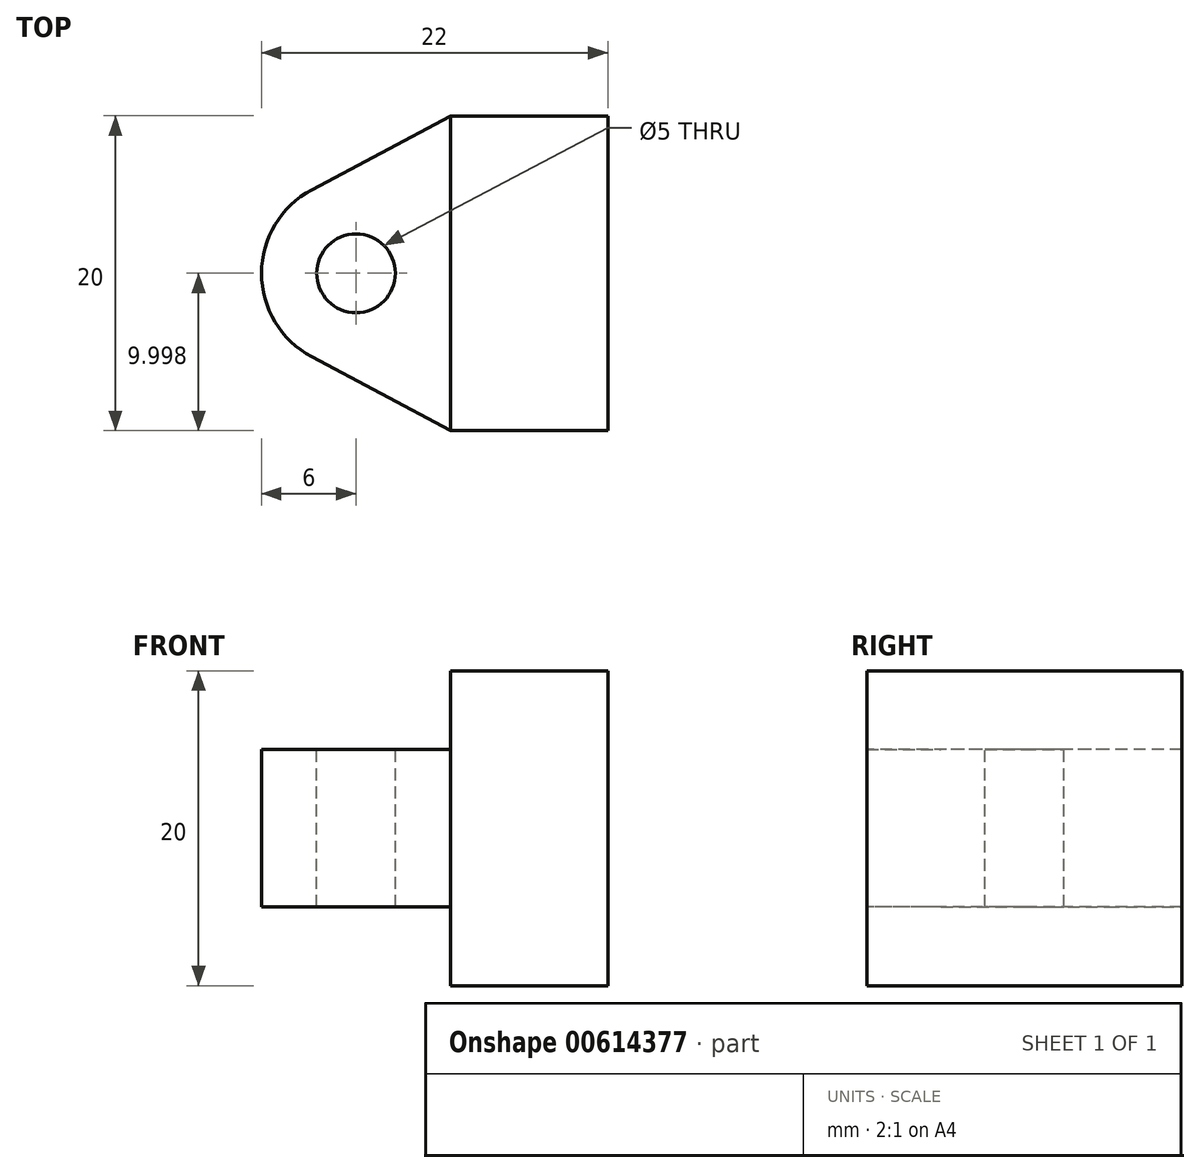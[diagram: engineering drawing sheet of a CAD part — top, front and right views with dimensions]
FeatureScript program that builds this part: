
annotation { "Feature Type Name" : "Feature", "Feature Type Description" : "" }
export const myFeature = defineFeature(function(context is Context, id is Id, definition is map)
    precondition{}
    {
        {
            var Q0;
            Q0=qCreatedBy(makeId("Right.planeOp"),FACE);
            var sketch = newSketch(context, id + "F0", { "sketchPlane" : qUnion([Q0])});
            skLineSegment(sketch, "E0", {"start": v(5.69, -2.66) * mm, "end": v(-14.31, -2.66) * mm});
            skLineSegment(sketch, "E1", {"start": v(-14.31, -2.66) * mm, "end": v(-14.31, -22.66) * mm});
            skLineSegment(sketch, "E2", {"start": v(-14.31, -22.66) * mm, "end": v(5.69, -22.66) * mm});
            skLineSegment(sketch, "E3", {"start": v(5.69, -22.66) * mm, "end": v(5.69, -2.66) * mm});
            skSolve(sketch);
        }
        {
            var Q0;
            Q0=makeQuery(id+"F0.imprint","IMPRINT",FACE,{"disambiguationData":[TD([[makeQuery(id+"F0.imprint","IMPRINT",EDGE,{"derivedFrom":sQuery(id+"F0.wireOp",EDGE,"E0")}),1.0]])]});
            extrude(context, id + "F1", {"entities" : qUnion([Q0]), "depth" : 10 * mm, "offsetDistance" : 25 * mm});
        }
        {
            var Q0;
            Q0=makeQuery(id+"F1.opExtrude","SWEPT_FACE",FACE,{"disambiguationData":[OSD([sQuery(id+"F0.wireOp",EDGE,"E1")])]});
            var sketch = newSketch(context, id + "F2", { "sketchPlane" : qUnion([Q0])});
            skLineSegment(sketch, "E4", {"start": v(0, -7.66) * mm, "end": v(-12, -7.66) * mm});
            skLineSegment(sketch, "E5", {"start": v(-12, -7.66) * mm, "end": v(-12, -17.66) * mm});
            skLineSegment(sketch, "E6", {"start": v(-12, -17.66) * mm, "end": v(0, -17.66) * mm});
            skLineSegment(sketch, "E7", {"start": v(0, -17.66) * mm, "end": v(0, -7.66) * mm});
            skSolve(sketch);
        }
        {
            var Q0;
            Q0=makeQuery(id+"F2.imprint","IMPRINT",FACE,{"disambiguationData":[TD([[makeQuery(id+"F2.imprint","IMPRINT",EDGE,{"derivedFrom":sQuery(id+"F2.wireOp",EDGE,"E4")}),1.0]])]});
            var Q1;
            Q1=makeQuery(id+"F1.opExtrude","SWEPT_FACE",FACE,{"disambiguationData":[OSD([sQuery(id+"F0.wireOp",EDGE,"E3")])]});
            extrude(context, id + "F3", {"entities" : qUnion([Q0]), "operationType" : NewBodyOperationType.ADD, "endBound" : BoundingType.UP_TO_SURFACE, "oppositeDirection" : true, "depth" : 25 * mm, "endBoundEntityFace" : qUnion([Q1]), "offsetDistance" : 25 * mm});
        }
        {
            var Q0;
            Q0=makeQuery(id+"F3.opExtrude","SWEPT_FACE",FACE,{"disambiguationData":[OSD([sQuery(id+"F2.wireOp",EDGE,"E4")])]});
            var sketch = newSketch(context, id + "F4", { "sketchPlane" : qUnion([Q0])});
            skCircle(sketch, "E8", {"center": v(-6, -4.31) * mm, "radius": 2.5 * mm});
            skPoint(sketch, "E8.centerSnap0", {"position": v(-12, -4.31) * mm});
            skArc(sketch, "E9", {"start": v(-8.82, 0.98) * mm, "mid": v(-12, -4.31) * mm, "end": v(-8.82, -9.6) * mm});
            skLineSegment(sketch, "E10", {"start": v(0, -14.31) * mm, "end": v(-8.82, -9.6) * mm});
            skLineSegment(sketch, "E11", {"start": v(0, 5.69) * mm, "end": v(-8.82, 0.98) * mm});
            skSolve(sketch);
        }
        {
            var Q0;
            {var subQ0=sQuery(id+"F4.wireOp",EDGE,"E11");Q0=makeQuery(id+"F4.imprint","IMPRINT",FACE,{"disambiguationData":[TD([[makeQuery(id+"F4.imprint","IMPRINT",EDGE,{"derivedFrom":subQ0}),-1.0]])]});}
            var Q1;
            {var subQ0=sQuery(id+"F4.wireOp",EDGE,"E10");Q1=makeQuery(id+"F4.imprint","IMPRINT",FACE,{"disambiguationData":[TD([[makeQuery(id+"F4.imprint","IMPRINT",EDGE,{"derivedFrom":subQ0}),1.0]])]});}
            extrude(context, id + "F5", {"entities" : qUnion([Q0, Q1]), "operationType" : NewBodyOperationType.REMOVE, "oppositeDirection" : true, "depth" : 25 * mm, "offsetDistance" : 25 * mm});
        }
        {
            var Q0;
            Q0=sQuery(id+"F4.wireOp",VERTEX,"E8.center");
            var Q1;
            Q1=makeQuery(id+"F1.opExtrude","SWEPT_BODY",BODY,{"disambiguationData":[OSD([sQuery(id+"F0.wireOp",EDGE,"E0"),sQuery(id+"F0.wireOp",EDGE,"E1"),sQuery(id+"F0.wireOp",EDGE,"E2"),sQuery(id+"F0.wireOp",EDGE,"E3")])]});
            hole(context, id + "F6", {"style" : HoleStyle.SIMPLE, "endStyle" : HoleEndStyle.THROUGH, "standardTappedOrClearance" : lookupTablePath({ "standard" : "ISO", "size" : "5", "type" : "Drilled" }), "standardBlindInLast" : lookupTablePath({ "standard" : "ISO", "size" : "5", "type" : "Drilled" }), "holeDiameter" : 5 * mm, "majorDiameter" : 5 * mm, "isTappedThrough" : true, "tappedDepth" : 12 * mm, "tapClearance" : 3, "locations" : qUnion([Q0]), "scope" : qUnion([Q1])});
        }
    });
